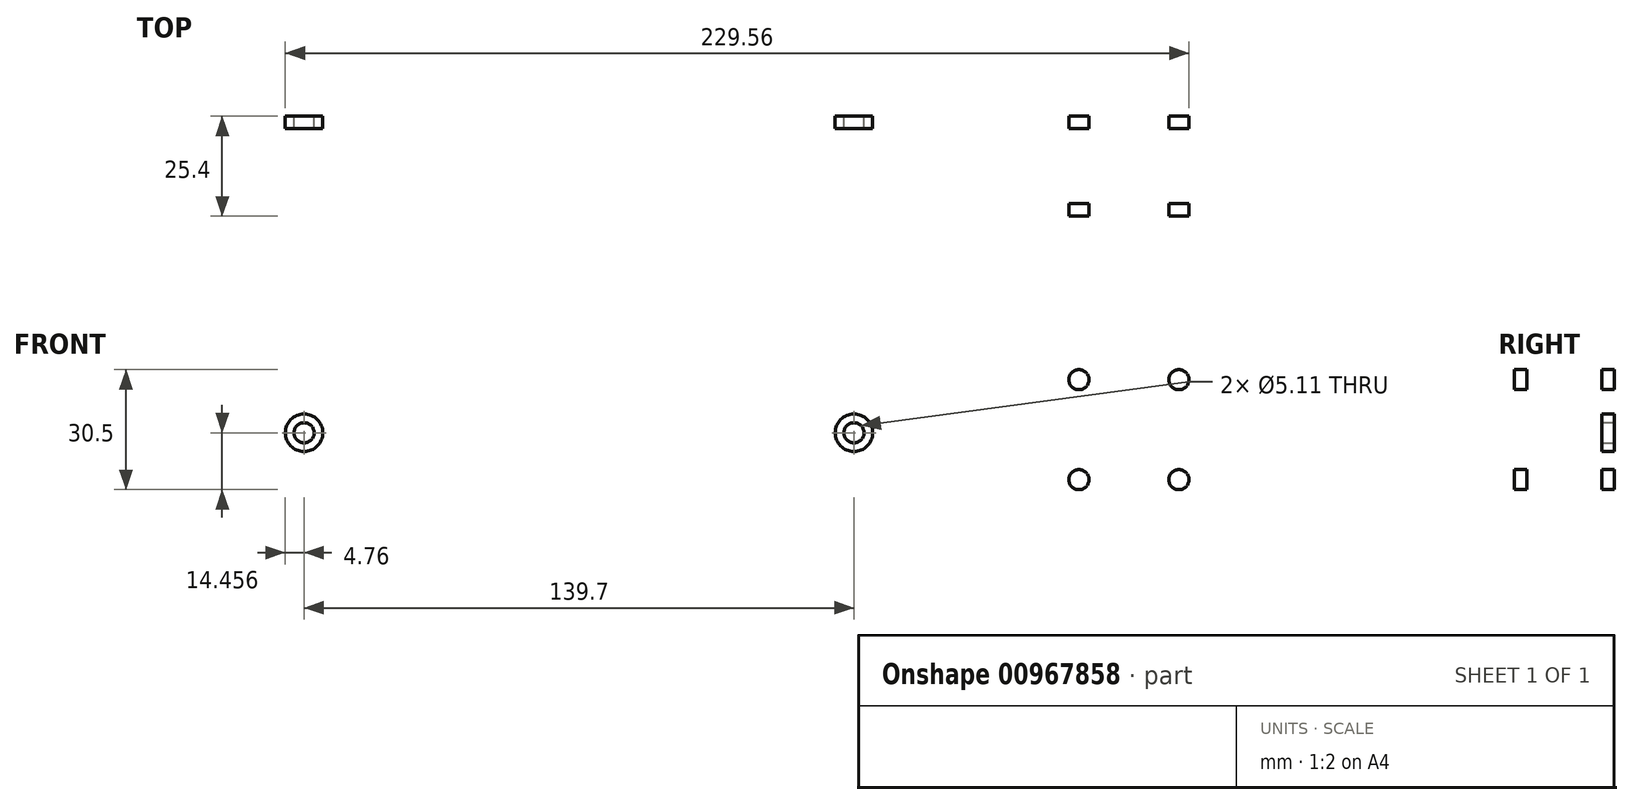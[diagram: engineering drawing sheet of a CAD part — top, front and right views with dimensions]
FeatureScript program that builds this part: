
annotation { "Feature Type Name" : "Feature", "Feature Type Description" : "" }
export const myFeature = defineFeature(function(context is Context, id is Id, definition is map)
    precondition{}
    {
        {
            var Q0;
            Q0=qCreatedBy(makeId("Front.planeOp"),FACE);
            var sketch = newSketch(context, id + "F0", { "sketchPlane" : qUnion([Q0])});
            skLineSegment(sketch, "E0.bottom", {"start": v(381, -25.4) * mm, "end": v(-381, -25.4) * mm});
            skLineSegment(sketch, "E0.top", {"start": v(381, 25.4) * mm, "end": v(-381, 25.4) * mm});
            skLineSegment(sketch, "E0.left", {"start": v(381, -25.4) * mm, "end": v(381, 25.4) * mm});
            skLineSegment(sketch, "E0.right", {"start": v(-381, -25.4) * mm, "end": v(-381, 25.4) * mm});
            skPoint(sketch, "E0.middle", {"position": v(0, 0) * mm});
            skLineSegment(sketch, "E1", {"start": v(-381, 0.8) * mm, "end": v(381, 0.8) * mm, "construction": true});
            skLineSegment(sketch, "E2", {"start": v(-381, -0.8) * mm, "end": v(381, -0.8) * mm, "construction": true});
            skLineSegment(sketch, "E3", {"start": v(0, 0.8) * mm, "end": v(0, -0.8) * mm, "construction": true});
            skCircle(sketch, "E4", {"center": v(-292.1, 0.8) * mm, "radius": 50.8 * mm, "construction": true});
            skCircle(sketch, "E5", {"center": v(292.1, 0.8) * mm, "radius": 50.8 * mm, "construction": true});
            skCircle(sketch, "E6", {"center": v(0, -0.8) * mm, "radius": 50.8 * mm, "construction": true});
            skLineSegment(sketch, "E7", {"start": v(-292.1, 0.8) * mm, "end": v(292.1, 0.8) * mm, "construction": true});
            skCircle(sketch, "E8", {"center": v(0, -0.8) * mm, "radius": 19.11 * mm});
            skCircle(sketch, "E9", {"center": v(-23.81, -0.8) * mm, "radius": 2.55 * mm});
            skCircle(sketch, "E10", {"center": v(23.81, -0.8) * mm, "radius": 2.55 * mm});
            skLineSegment(sketch, "E11", {"start": v(-23.81, -0.8) * mm, "end": v(23.81, -0.8) * mm});
            skLineSegment(sketch, "E12", {"start": v(23.81, -0.8) * mm, "end": v(-23.81, -0.8) * mm, "construction": true});
            skLineSegment(sketch, "E13.bottom", {"start": v(-273.05, -16.68) * mm, "end": v(-311.15, -16.68) * mm});
            skLineSegment(sketch, "E13.top", {"start": v(-273.05, 18.27) * mm, "end": v(-311.15, 18.27) * mm});
            skLineSegment(sketch, "E13.left", {"start": v(-269.88, -16.68) * mm, "end": v(-269.88, 18.27) * mm, "construction": true});
            skLineSegment(sketch, "E13.right", {"start": v(-314.33, -16.68) * mm, "end": v(-314.33, 18.27) * mm, "construction": true});
            skLineSegment(sketch, "E14", {"start": v(-314.33, 15.1) * mm, "end": v(-314.33, 3.35) * mm});
            skLineSegment(sketch, "E15", {"start": v(-314.33, 3.35) * mm, "end": v(-323.85, 3.35) * mm});
            skArc(sketch, "E16", {"start": v(-323.85, 3.35) * mm, "mid": v(-326.4, 0.8) * mm, "end": v(-323.85, -1.76) * mm});
            skLineSegment(sketch, "E17", {"start": v(-323.85, -1.76) * mm, "end": v(-314.33, -1.76) * mm});
            skLineSegment(sketch, "E18", {"start": v(-314.33, -1.76) * mm, "end": v(-314.33, -13.5) * mm});
            skLineSegment(sketch, "E19", {"start": v(-269.88, 3.35) * mm, "end": v(-260.35, 3.35) * mm});
            skLineSegment(sketch, "E20", {"start": v(-269.88, -1.76) * mm, "end": v(-260.35, -1.76) * mm});
            skArc(sketch, "E21", {"start": v(-260.35, -1.76) * mm, "mid": v(-257.8, 0.8) * mm, "end": v(-260.35, 3.35) * mm});
            skCircle(sketch, "E22", {"center": v(-247.65, 0.8) * mm, "radius": 2.55 * mm});
            skLineSegment(sketch, "E23", {"start": v(-269.88, 15.1) * mm, "end": v(-269.88, 3.35) * mm});
            skLineSegment(sketch, "E24", {"start": v(-269.88, -1.76) * mm, "end": v(-269.88, -13.5) * mm});
            skPoint(sketch, "E25.visualSharp", {"position": v(-314.33, 18.27) * mm});
            skArc(sketch, "E25.filletArc", {"start": v(-311.15, 18.27) * mm, "mid": v(-313.4, 17.34) * mm, "end": v(-314.33, 15.1) * mm});
            skPoint(sketch, "E26.visualSharp", {"position": v(-269.88, 18.27) * mm});
            skArc(sketch, "E26.filletArc", {"start": v(-269.88, 15.1) * mm, "mid": v(-270.8, 17.34) * mm, "end": v(-273.05, 18.27) * mm});
            skPoint(sketch, "E27.visualSharp", {"position": v(-269.88, -16.68) * mm});
            skArc(sketch, "E27.filletArc", {"start": v(-273.05, -16.68) * mm, "mid": v(-270.8, -15.75) * mm, "end": v(-269.88, -13.5) * mm});
            skPoint(sketch, "E28.visualSharp", {"position": v(-314.33, -16.68) * mm});
            skArc(sketch, "E28.filletArc", {"start": v(-314.33, -13.5) * mm, "mid": v(-313.4, -15.75) * mm, "end": v(-311.15, -16.68) * mm});
            skArc(sketch, "E29.MirrorCS", {"start": v(311.15, 18.27) * mm, "mid": v(313.4, 17.34) * mm, "end": v(314.33, 15.1) * mm});
            skArc(sketch, "E30.MirrorCS", {"start": v(323.85, 3.35) * mm, "mid": v(326.4, 0.8) * mm, "end": v(323.85, -1.76) * mm});
            skArc(sketch, "E31.MirrorCS", {"start": v(269.88, 15.1) * mm, "mid": v(270.8, 17.34) * mm, "end": v(273.05, 18.27) * mm});
            skArc(sketch, "E32.MirrorCS", {"start": v(314.33, -13.5) * mm, "mid": v(313.4, -15.75) * mm, "end": v(311.15, -16.68) * mm});
            skLineSegment(sketch, "E33.MirrorCS", {"start": v(314.33, 3.35) * mm, "end": v(323.85, 3.35) * mm});
            skLineSegment(sketch, "E34.MirrorCS", {"start": v(323.85, -1.76) * mm, "end": v(314.33, -1.76) * mm});
            skArc(sketch, "E35.MirrorCS", {"start": v(260.35, -1.76) * mm, "mid": v(257.8, 0.8) * mm, "end": v(260.35, 3.35) * mm});
            skArc(sketch, "E36.MirrorCS", {"start": v(273.05, -16.68) * mm, "mid": v(270.8, -15.75) * mm, "end": v(269.88, -13.5) * mm});
            skLineSegment(sketch, "E37.MirrorCS", {"start": v(269.88, 3.35) * mm, "end": v(260.35, 3.35) * mm});
            skCircle(sketch, "E38.MirrorC", {"center": v(247.65, 0.8) * mm, "radius": 2.55 * mm});
            skLineSegment(sketch, "E39.MirrorCS", {"start": v(314.33, -1.76) * mm, "end": v(314.33, -13.5) * mm});
            skLineSegment(sketch, "E40.MirrorCS", {"start": v(269.88, 15.1) * mm, "end": v(269.88, 3.35) * mm});
            skLineSegment(sketch, "E41.MirrorCS", {"start": v(314.33, 15.1) * mm, "end": v(314.33, 3.35) * mm});
            skLineSegment(sketch, "E42.MirrorCS", {"start": v(269.88, -1.76) * mm, "end": v(269.88, -13.5) * mm});
            skPoint(sketch, "E43.MirrorP", {"position": v(314.33, 18.27) * mm});
            skLineSegment(sketch, "E44.MirrorCS", {"start": v(269.88, -1.76) * mm, "end": v(260.35, -1.76) * mm});
            skPoint(sketch, "E45.MirrorP", {"position": v(314.33, -16.68) * mm});
            skLineSegment(sketch, "E46.MirrorCS", {"start": v(269.88, -16.68) * mm, "end": v(269.88, 18.27) * mm, "construction": true});
            skLineSegment(sketch, "E47.MirrorCS", {"start": v(314.33, -16.68) * mm, "end": v(314.33, 18.27) * mm, "construction": true});
            skPoint(sketch, "E48.MirrorP", {"position": v(269.88, 18.27) * mm});
            skLineSegment(sketch, "E49.MirrorCS", {"start": v(273.05, -16.68) * mm, "end": v(311.15, -16.68) * mm});
            skPoint(sketch, "E50.MirrorP", {"position": v(269.88, -16.68) * mm});
            skLineSegment(sketch, "E51.MirrorCS", {"start": v(273.05, 18.27) * mm, "end": v(311.15, 18.27) * mm});
            skCircle(sketch, "E52", {"center": v(69.85, -0.8) * mm, "radius": 2.55 * mm});
            skCircle(sketch, "E53", {"center": v(-69.85, -0.8) * mm, "radius": 2.55 * mm});
            skLineSegment(sketch, "E54", {"start": v(-69.85, -0.8) * mm, "end": v(69.85, -0.8) * mm, "construction": true});
            skSolve(sketch);
        }
        {
            var Q0;
            Q0=qSketchRegion(id+"F0",true);
            extrude(context, id + "F1", {"entities" : qUnion([Q0]), "depth" : 25.4 * mm, "offsetDistance" : 25.4 * mm});
        }
        {
            var Q0;
            Q0=makeQuery(id+"F1.opExtrude","SWEPT_FACE",FACE,{"disambiguationData":[OSD([sQuery(id+"F0.wireOp",EDGE,"E0.right")])]});
            var sketch = newSketch(context, id + "F2", { "sketchPlane" : qUnion([Q0])});
            skLineSegment(sketch, "E55.0", {"start": v(22.23, 22.23) * mm, "end": v(3.18, 22.23) * mm});
            skLineSegment(sketch, "E55.1", {"start": v(22.23, -22.22) * mm, "end": v(22.23, 22.23) * mm});
            skLineSegment(sketch, "E55.2", {"start": v(22.23, -22.22) * mm, "end": v(3.18, -22.22) * mm});
            skLineSegment(sketch, "E55.3", {"start": v(3.18, -22.22) * mm, "end": v(3.18, 22.23) * mm});
            skSolve(sketch);
        }
        {
            var Q0;
            Q0=makeQuery(id+"F2.imprint","IMPRINT",FACE,{"disambiguationData":[TD([[makeQuery(id+"F2.imprint","IMPRINT",EDGE,{"derivedFrom":sQuery(id+"F2.wireOp",EDGE,"E55.0")}),1.0]])]});
            extrude(context, id + "F3", {"entities" : qUnion([Q0]), "operationType" : NewBodyOperationType.REMOVE, "oppositeDirection" : true, "depth" : 762 * mm, "offsetDistance" : 25.4 * mm});
        }
        {
            var Q0;
            Q0=makeQuery(id+"F1.opExtrude","SWEPT_FACE",FACE,{"disambiguationData":[OSD([sQuery(id+"F0.wireOp",EDGE,"E0.top")])]});
            var sketch = newSketch(context, id + "F4", { "sketchPlane" : qUnion([Q0])});
            skCircle(sketch, "E56", {"center": v(-368.3, -12.7) * mm, "radius": 2.55 * mm});
            skPoint(sketch, "E56.centerSnap0", {"position": v(-381, -12.7) * mm});
            skCircle(sketch, "E57.1.0.0", {"center": v(-342.9, -12.7) * mm, "radius": 2.55 * mm});
            skCircle(sketch, "E57.2.0.0", {"center": v(-317.5, -12.7) * mm, "radius": 2.55 * mm});
            skCircle(sketch, "E57.3.0.0", {"center": v(-292.1, -12.7) * mm, "radius": 2.55 * mm});
            skCircle(sketch, "E57.4.0.0", {"center": v(-266.7, -12.7) * mm, "radius": 2.55 * mm});
            skCircle(sketch, "E57.5.0.0", {"center": v(-241.3, -12.7) * mm, "radius": 2.55 * mm});
            skCircle(sketch, "E57.6.0.0", {"center": v(-215.9, -12.7) * mm, "radius": 2.55 * mm});
            skCircle(sketch, "E57.7.0.0", {"center": v(-190.5, -12.7) * mm, "radius": 2.55 * mm});
            skCircle(sketch, "E57.8.0.0", {"center": v(-165.1, -12.7) * mm, "radius": 2.55 * mm});
            skCircle(sketch, "E57.9.0.0", {"center": v(-139.7, -12.7) * mm, "radius": 2.55 * mm});
            skCircle(sketch, "E57.10.0.0", {"center": v(-114.3, -12.7) * mm, "radius": 2.55 * mm});
            skCircle(sketch, "E57.11.0.0", {"center": v(-88.9, -12.7) * mm, "radius": 2.55 * mm});
            skCircle(sketch, "E57.12.0.0", {"center": v(-63.5, -12.7) * mm, "radius": 2.55 * mm});
            skCircle(sketch, "E57.13.0.0", {"center": v(-38.1, -12.7) * mm, "radius": 2.55 * mm});
            skCircle(sketch, "E57.14.0.0", {"center": v(-12.7, -12.7) * mm, "radius": 2.55 * mm});
            skCircle(sketch, "E57.15.0.0", {"center": v(12.7, -12.7) * mm, "radius": 2.55 * mm});
            skCircle(sketch, "E57.16.0.0", {"center": v(38.1, -12.7) * mm, "radius": 2.55 * mm});
            skCircle(sketch, "E57.17.0.0", {"center": v(63.5, -12.7) * mm, "radius": 2.55 * mm});
            skCircle(sketch, "E57.18.0.0", {"center": v(88.9, -12.7) * mm, "radius": 2.55 * mm});
            skCircle(sketch, "E57.19.0.0", {"center": v(114.3, -12.7) * mm, "radius": 2.55 * mm});
            skCircle(sketch, "E57.20.0.0", {"center": v(139.7, -12.7) * mm, "radius": 2.55 * mm});
            skCircle(sketch, "E57.21.0.0", {"center": v(165.1, -12.7) * mm, "radius": 2.55 * mm});
            skCircle(sketch, "E57.22.0.0", {"center": v(190.5, -12.7) * mm, "radius": 2.55 * mm});
            skCircle(sketch, "E57.23.0.0", {"center": v(215.9, -12.7) * mm, "radius": 2.55 * mm});
            skCircle(sketch, "E57.24.0.0", {"center": v(241.3, -12.7) * mm, "radius": 2.55 * mm});
            skCircle(sketch, "E57.25.0.0", {"center": v(266.7, -12.7) * mm, "radius": 2.55 * mm});
            skCircle(sketch, "E57.26.0.0", {"center": v(292.1, -12.7) * mm, "radius": 2.55 * mm});
            skCircle(sketch, "E57.27.0.0", {"center": v(317.5, -12.7) * mm, "radius": 2.55 * mm});
            skCircle(sketch, "E57.28.0.0", {"center": v(342.9, -12.7) * mm, "radius": 2.55 * mm});
            skCircle(sketch, "E57.29.0.0", {"center": v(368.3, -12.7) * mm, "radius": 2.55 * mm});
            skLineSegment(sketch, "E57.direction1", {"start": v(-368.3, -12.7) * mm, "end": v(-342.9, -12.7) * mm, "construction": true});
            skSolve(sketch);
        }
        {
            var Q0;
            Q0=sQuery(id+"F4.wireOp",VERTEX,"E57.22.0.0.center");
            var Q1;
            Q1=sQuery(id+"F4.wireOp",VERTEX,"E57.16.0.0.center");
            var Q2;
            Q2=sQuery(id+"F4.wireOp",VERTEX,"E57.23.0.0.center");
            var Q3;
            Q3=sQuery(id+"F4.wireOp",VERTEX,"E57.17.0.0.center");
            var Q4;
            Q4=sQuery(id+"F4.wireOp",VERTEX,"E57.26.0.0.center");
            var Q5;
            Q5=sQuery(id+"F4.wireOp",VERTEX,"E57.20.0.0.center");
            var Q6;
            Q6=sQuery(id+"F4.wireOp",VERTEX,"E57.13.0.0.center");
            var Q7;
            Q7=sQuery(id+"F4.wireOp",VERTEX,"E57.29.0.0.center");
            var Q8;
            Q8=sQuery(id+"F4.wireOp",VERTEX,"E57.24.0.0.center");
            var Q9;
            Q9=sQuery(id+"F4.wireOp",VERTEX,"E57.10.0.0.center");
            var Q10;
            Q10=sQuery(id+"F4.wireOp",VERTEX,"E57.18.0.0.center");
            var Q11;
            Q11=sQuery(id+"F4.wireOp",VERTEX,"E57.11.0.0.center");
            var Q12;
            Q12=sQuery(id+"F4.wireOp",VERTEX,"E57.27.0.0.center");
            var Q13;
            Q13=sQuery(id+"F4.wireOp",VERTEX,"E57.12.0.0.center");
            var Q14;
            Q14=sQuery(id+"F4.wireOp",VERTEX,"E57.14.0.0.center");
            var Q15;
            Q15=sQuery(id+"F4.wireOp",VERTEX,"E57.1.0.0.center");
            var Q16;
            Q16=sQuery(id+"F4.wireOp",VERTEX,"E57.2.0.0.center");
            var Q17;
            Q17=sQuery(id+"F4.wireOp",VERTEX,"E57.3.0.0.center");
            var Q18;
            Q18=sQuery(id+"F4.wireOp",VERTEX,"E57.4.0.0.center");
            var Q19;
            Q19=sQuery(id+"F4.wireOp",VERTEX,"E57.5.0.0.center");
            var Q20;
            Q20=sQuery(id+"F4.wireOp",VERTEX,"E57.6.0.0.center");
            var Q21;
            Q21=sQuery(id+"F4.wireOp",VERTEX,"E57.7.0.0.center");
            var Q22;
            Q22=sQuery(id+"F4.wireOp",VERTEX,"E57.8.0.0.center");
            var Q23;
            Q23=sQuery(id+"F4.wireOp",VERTEX,"E57.9.0.0.center");
            var Q24;
            Q24=sQuery(id+"F4.wireOp",VERTEX,"E57.25.0.0.center");
            var Q25;
            Q25=sQuery(id+"F4.wireOp",VERTEX,"E57.21.0.0.center");
            var Q26;
            Q26=sQuery(id+"F4.wireOp",VERTEX,"E57.19.0.0.center");
            var Q27;
            Q27=sQuery(id+"F4.wireOp",VERTEX,"E57.28.0.0.center");
            var Q28;
            Q28=sQuery(id+"F4.wireOp",VERTEX,"E57.15.0.0.center");
            var Q29;
            Q29=sQuery(id+"F4.wireOp",VERTEX,"E56.center");
            var Q30;
            Q30=makeQuery(id+"F1.opExtrude","SWEPT_BODY",BODY,{"disambiguationData":[OSD([sQuery(id+"F0.wireOp",EDGE,"E0.bottom"),sQuery(id+"F0.wireOp",EDGE,"E0.top"),sQuery(id+"F0.wireOp",EDGE,"E0.right"),sQuery(id+"F0.wireOp",EDGE,"E8"),sQuery(id+"F0.wireOp",EDGE,"E9"),sQuery(id+"F0.wireOp",EDGE,"E10"),sQuery(id+"F0.wireOp",EDGE,"E13.bottom"),sQuery(id+"F0.wireOp",EDGE,"E13.top"),sQuery(id+"F0.wireOp",EDGE,"E14"),sQuery(id+"F0.wireOp",EDGE,"E15"),sQuery(id+"F0.wireOp",EDGE,"E16"),sQuery(id+"F0.wireOp",EDGE,"E17"),sQuery(id+"F0.wireOp",EDGE,"E18"),sQuery(id+"F0.wireOp",EDGE,"E19"),sQuery(id+"F0.wireOp",EDGE,"E20"),sQuery(id+"F0.wireOp",EDGE,"E21"),sQuery(id+"F0.wireOp",EDGE,"E22"),sQuery(id+"F0.wireOp",EDGE,"E23"),sQuery(id+"F0.wireOp",EDGE,"E24"),sQuery(id+"F0.wireOp",EDGE,"E25.filletArc"),sQuery(id+"F0.wireOp",EDGE,"E26.filletArc"),sQuery(id+"F0.wireOp",EDGE,"E27.filletArc"),sQuery(id+"F0.wireOp",EDGE,"E28.filletArc"),sQuery(id+"F0.wireOp",EDGE,"E29.MirrorCS"),sQuery(id+"F0.wireOp",EDGE,"E30.MirrorCS"),sQuery(id+"F0.wireOp",EDGE,"E31.MirrorCS"),sQuery(id+"F0.wireOp",EDGE,"E32.MirrorCS"),sQuery(id+"F0.wireOp",EDGE,"E33.MirrorCS"),sQuery(id+"F0.wireOp",EDGE,"E34.MirrorCS"),sQuery(id+"F0.wireOp",EDGE,"E35.MirrorCS"),sQuery(id+"F0.wireOp",EDGE,"E36.MirrorCS"),sQuery(id+"F0.wireOp",EDGE,"E37.MirrorCS"),sQuery(id+"F0.wireOp",EDGE,"E38.MirrorC"),sQuery(id+"F0.wireOp",EDGE,"E39.MirrorCS"),sQuery(id+"F0.wireOp",EDGE,"E40.MirrorCS"),sQuery(id+"F0.wireOp",EDGE,"E41.MirrorCS"),sQuery(id+"F0.wireOp",EDGE,"E42.MirrorCS"),sQuery(id+"F0.wireOp",EDGE,"E44.MirrorCS"),sQuery(id+"F0.wireOp",EDGE,"E49.MirrorCS"),sQuery(id+"F0.wireOp",EDGE,"E51.MirrorCS"),sQuery(id+"F0.wireOp",EDGE,"E0.left"),sQuery(id+"F0.wireOp",EDGE,"E52"),sQuery(id+"F0.wireOp",EDGE,"E53")])]});
            hole(context, id + "F5", {"style" : HoleStyle.SIMPLE, "endStyle" : HoleEndStyle.BLIND, "holeDiameter" : 5.1 * mm, "majorDiameter" : 6.35 * mm, "holeDepth" : 50.8 * mm, "isTappedThrough" : true, "tappedDepth" : 12.7 * mm, "tapClearance" : 3, "startFromSketch" : true, "locations" : qUnion([Q0, Q1, Q2, Q3, Q4, Q5, Q6, Q7, Q8, Q9, Q10, Q11, Q12, Q13, Q14, Q15, Q16, Q17, Q18, Q19, Q20, Q21, Q22, Q23, Q24, Q25, Q26, Q27, Q28, Q29]), "scope" : qUnion([Q30])});
        }
        {
            var Q0;
            Q0=makeQuery(id+"F1.opExtrude","CAP_FACE",FACE,{"disambiguationData":[OSD([sQuery(id+"F0.wireOp",EDGE,"E0.bottom"),sQuery(id+"F0.wireOp",EDGE,"E0.top"),sQuery(id+"F0.wireOp",EDGE,"E0.right"),sQuery(id+"F0.wireOp",EDGE,"E8"),sQuery(id+"F0.wireOp",EDGE,"E9"),sQuery(id+"F0.wireOp",EDGE,"E10"),sQuery(id+"F0.wireOp",EDGE,"E13.bottom"),sQuery(id+"F0.wireOp",EDGE,"E13.top"),sQuery(id+"F0.wireOp",EDGE,"E14"),sQuery(id+"F0.wireOp",EDGE,"E15"),sQuery(id+"F0.wireOp",EDGE,"E16"),sQuery(id+"F0.wireOp",EDGE,"E17"),sQuery(id+"F0.wireOp",EDGE,"E18"),sQuery(id+"F0.wireOp",EDGE,"E19"),sQuery(id+"F0.wireOp",EDGE,"E20"),sQuery(id+"F0.wireOp",EDGE,"E21"),sQuery(id+"F0.wireOp",EDGE,"E22"),sQuery(id+"F0.wireOp",EDGE,"E23"),sQuery(id+"F0.wireOp",EDGE,"E24"),sQuery(id+"F0.wireOp",EDGE,"E25.filletArc"),sQuery(id+"F0.wireOp",EDGE,"E26.filletArc"),sQuery(id+"F0.wireOp",EDGE,"E27.filletArc"),sQuery(id+"F0.wireOp",EDGE,"E28.filletArc"),sQuery(id+"F0.wireOp",EDGE,"E29.MirrorCS"),sQuery(id+"F0.wireOp",EDGE,"E30.MirrorCS"),sQuery(id+"F0.wireOp",EDGE,"E31.MirrorCS"),sQuery(id+"F0.wireOp",EDGE,"E32.MirrorCS"),sQuery(id+"F0.wireOp",EDGE,"E33.MirrorCS"),sQuery(id+"F0.wireOp",EDGE,"E34.MirrorCS"),sQuery(id+"F0.wireOp",EDGE,"E35.MirrorCS"),sQuery(id+"F0.wireOp",EDGE,"E36.MirrorCS"),sQuery(id+"F0.wireOp",EDGE,"E37.MirrorCS"),sQuery(id+"F0.wireOp",EDGE,"E38.MirrorC"),sQuery(id+"F0.wireOp",EDGE,"E39.MirrorCS"),sQuery(id+"F0.wireOp",EDGE,"E40.MirrorCS"),sQuery(id+"F0.wireOp",EDGE,"E41.MirrorCS"),sQuery(id+"F0.wireOp",EDGE,"E42.MirrorCS"),sQuery(id+"F0.wireOp",EDGE,"E44.MirrorCS"),sQuery(id+"F0.wireOp",EDGE,"E49.MirrorCS"),sQuery(id+"F0.wireOp",EDGE,"E51.MirrorCS"),sQuery(id+"F0.wireOp",EDGE,"E0.left"),sQuery(id+"F0.wireOp",EDGE,"E52"),sQuery(id+"F0.wireOp",EDGE,"E53")])],"isStart":false});
            var sketch = newSketch(context, id + "F6", { "sketchPlane" : qUnion([Q0])});
            skCircle(sketch, "E58", {"center": v(-69.85, -0.8) * mm, "radius": 4.76 * mm});
            skCircle(sketch, "E59", {"center": v(69.85, -0.8) * mm, "radius": 4.76 * mm});
            skSolve(sketch);
        }
        {
            var Q0;
            Q0=sQuery(id+"F6.wireOp",VERTEX,"E58.center");
            var Q1;
            Q1=sQuery(id+"F6.wireOp",VERTEX,"E59.center");
            var Q2;
            Q2=makeQuery(id+"F1.opExtrude","SWEPT_BODY",BODY,{"disambiguationData":[OSD([sQuery(id+"F0.wireOp",EDGE,"E0.bottom"),sQuery(id+"F0.wireOp",EDGE,"E0.top"),sQuery(id+"F0.wireOp",EDGE,"E0.right"),sQuery(id+"F0.wireOp",EDGE,"E8"),sQuery(id+"F0.wireOp",EDGE,"E9"),sQuery(id+"F0.wireOp",EDGE,"E10"),sQuery(id+"F0.wireOp",EDGE,"E13.bottom"),sQuery(id+"F0.wireOp",EDGE,"E13.top"),sQuery(id+"F0.wireOp",EDGE,"E14"),sQuery(id+"F0.wireOp",EDGE,"E15"),sQuery(id+"F0.wireOp",EDGE,"E16"),sQuery(id+"F0.wireOp",EDGE,"E17"),sQuery(id+"F0.wireOp",EDGE,"E18"),sQuery(id+"F0.wireOp",EDGE,"E19"),sQuery(id+"F0.wireOp",EDGE,"E20"),sQuery(id+"F0.wireOp",EDGE,"E21"),sQuery(id+"F0.wireOp",EDGE,"E22"),sQuery(id+"F0.wireOp",EDGE,"E23"),sQuery(id+"F0.wireOp",EDGE,"E24"),sQuery(id+"F0.wireOp",EDGE,"E25.filletArc"),sQuery(id+"F0.wireOp",EDGE,"E26.filletArc"),sQuery(id+"F0.wireOp",EDGE,"E27.filletArc"),sQuery(id+"F0.wireOp",EDGE,"E28.filletArc"),sQuery(id+"F0.wireOp",EDGE,"E29.MirrorCS"),sQuery(id+"F0.wireOp",EDGE,"E30.MirrorCS"),sQuery(id+"F0.wireOp",EDGE,"E31.MirrorCS"),sQuery(id+"F0.wireOp",EDGE,"E32.MirrorCS"),sQuery(id+"F0.wireOp",EDGE,"E33.MirrorCS"),sQuery(id+"F0.wireOp",EDGE,"E34.MirrorCS"),sQuery(id+"F0.wireOp",EDGE,"E35.MirrorCS"),sQuery(id+"F0.wireOp",EDGE,"E36.MirrorCS"),sQuery(id+"F0.wireOp",EDGE,"E37.MirrorCS"),sQuery(id+"F0.wireOp",EDGE,"E38.MirrorC"),sQuery(id+"F0.wireOp",EDGE,"E39.MirrorCS"),sQuery(id+"F0.wireOp",EDGE,"E40.MirrorCS"),sQuery(id+"F0.wireOp",EDGE,"E41.MirrorCS"),sQuery(id+"F0.wireOp",EDGE,"E42.MirrorCS"),sQuery(id+"F0.wireOp",EDGE,"E44.MirrorCS"),sQuery(id+"F0.wireOp",EDGE,"E49.MirrorCS"),sQuery(id+"F0.wireOp",EDGE,"E51.MirrorCS"),sQuery(id+"F0.wireOp",EDGE,"E0.left"),sQuery(id+"F0.wireOp",EDGE,"E52"),sQuery(id+"F0.wireOp",EDGE,"E53")])]});
            hole(context, id + "F7", {"style" : HoleStyle.SIMPLE, "endStyle" : HoleEndStyle.BLIND, "holeDiameter" : 9.52 * mm, "majorDiameter" : 6.35 * mm, "holeDepth" : 3.17 * mm, "isTappedThrough" : true, "tappedDepth" : 12.7 * mm, "tapClearance" : 3, "startFromSketch" : true, "locations" : qUnion([Q0, Q1]), "scope" : qUnion([Q2])});
        }
        {
            var Q0;
            Q0=makeQuery(id+"F1.opExtrude","CAP_FACE",FACE,{"disambiguationData":[OSD([sQuery(id+"F0.wireOp",EDGE,"E0.bottom"),sQuery(id+"F0.wireOp",EDGE,"E0.top"),sQuery(id+"F0.wireOp",EDGE,"E0.right"),sQuery(id+"F0.wireOp",EDGE,"E8"),sQuery(id+"F0.wireOp",EDGE,"E9"),sQuery(id+"F0.wireOp",EDGE,"E10"),sQuery(id+"F0.wireOp",EDGE,"E13.bottom"),sQuery(id+"F0.wireOp",EDGE,"E13.top"),sQuery(id+"F0.wireOp",EDGE,"E14"),sQuery(id+"F0.wireOp",EDGE,"E15"),sQuery(id+"F0.wireOp",EDGE,"E16"),sQuery(id+"F0.wireOp",EDGE,"E17"),sQuery(id+"F0.wireOp",EDGE,"E18"),sQuery(id+"F0.wireOp",EDGE,"E19"),sQuery(id+"F0.wireOp",EDGE,"E20"),sQuery(id+"F0.wireOp",EDGE,"E21"),sQuery(id+"F0.wireOp",EDGE,"E22"),sQuery(id+"F0.wireOp",EDGE,"E23"),sQuery(id+"F0.wireOp",EDGE,"E24"),sQuery(id+"F0.wireOp",EDGE,"E25.filletArc"),sQuery(id+"F0.wireOp",EDGE,"E26.filletArc"),sQuery(id+"F0.wireOp",EDGE,"E27.filletArc"),sQuery(id+"F0.wireOp",EDGE,"E28.filletArc"),sQuery(id+"F0.wireOp",EDGE,"E29.MirrorCS"),sQuery(id+"F0.wireOp",EDGE,"E30.MirrorCS"),sQuery(id+"F0.wireOp",EDGE,"E31.MirrorCS"),sQuery(id+"F0.wireOp",EDGE,"E32.MirrorCS"),sQuery(id+"F0.wireOp",EDGE,"E33.MirrorCS"),sQuery(id+"F0.wireOp",EDGE,"E34.MirrorCS"),sQuery(id+"F0.wireOp",EDGE,"E35.MirrorCS"),sQuery(id+"F0.wireOp",EDGE,"E36.MirrorCS"),sQuery(id+"F0.wireOp",EDGE,"E37.MirrorCS"),sQuery(id+"F0.wireOp",EDGE,"E38.MirrorC"),sQuery(id+"F0.wireOp",EDGE,"E39.MirrorCS"),sQuery(id+"F0.wireOp",EDGE,"E40.MirrorCS"),sQuery(id+"F0.wireOp",EDGE,"E41.MirrorCS"),sQuery(id+"F0.wireOp",EDGE,"E42.MirrorCS"),sQuery(id+"F0.wireOp",EDGE,"E44.MirrorCS"),sQuery(id+"F0.wireOp",EDGE,"E49.MirrorCS"),sQuery(id+"F0.wireOp",EDGE,"E51.MirrorCS"),sQuery(id+"F0.wireOp",EDGE,"E0.left"),sQuery(id+"F0.wireOp",EDGE,"E52"),sQuery(id+"F0.wireOp",EDGE,"E53")])],"isStart":false});
            var sketch = newSketch(context, id + "F8", { "sketchPlane" : qUnion([Q0])});
            skLineSegment(sketch, "E60.bottom", {"start": v(-152.4, 12.7) * mm, "end": v(-127, 12.7) * mm, "construction": true});
            skLineSegment(sketch, "E60.top", {"start": v(-152.4, -12.7) * mm, "end": v(-127, -12.7) * mm, "construction": true});
            skLineSegment(sketch, "E60.left", {"start": v(-152.4, 12.7) * mm, "end": v(-152.4, -12.7) * mm, "construction": true});
            skLineSegment(sketch, "E60.right", {"start": v(-127, 12.7) * mm, "end": v(-127, -12.7) * mm, "construction": true});
            skPoint(sketch, "E60.middle", {"position": v(-139.7, 0) * mm});
            skCircle(sketch, "E61", {"center": v(-152.4, 12.7) * mm, "radius": 2.55 * mm});
            skCircle(sketch, "E62", {"center": v(-127, 12.7) * mm, "radius": 2.55 * mm});
            skCircle(sketch, "E63", {"center": v(-152.4, -12.7) * mm, "radius": 2.55 * mm});
            skCircle(sketch, "E64", {"center": v(-127, -12.7) * mm, "radius": 2.55 * mm});
            skLineSegment(sketch, "E65", {"start": v(0, 25.4) * mm, "end": v(0, -25.4) * mm, "construction": true});
            skCircle(sketch, "E66.MirrorC", {"center": v(127, 12.7) * mm, "radius": 2.55 * mm});
            skCircle(sketch, "E67.MirrorC", {"center": v(152.4, -12.7) * mm, "radius": 2.55 * mm});
            skCircle(sketch, "E68.MirrorC", {"center": v(127, -12.7) * mm, "radius": 2.55 * mm});
            skCircle(sketch, "E69.MirrorC", {"center": v(152.4, 12.7) * mm, "radius": 2.55 * mm});
            skLineSegment(sketch, "E70.MirrorCS", {"start": v(127, 12.7) * mm, "end": v(127, -12.7) * mm, "construction": true});
            skLineSegment(sketch, "E71.MirrorCS", {"start": v(152.4, 12.7) * mm, "end": v(127, 12.7) * mm, "construction": true});
            skLineSegment(sketch, "E72.MirrorCS", {"start": v(152.4, 12.7) * mm, "end": v(152.4, -12.7) * mm, "construction": true});
            skPoint(sketch, "E73.MirrorP", {"position": v(139.7, 0) * mm});
            skLineSegment(sketch, "E74.MirrorCS", {"start": v(152.4, -12.7) * mm, "end": v(127, -12.7) * mm, "construction": true});
            skSolve(sketch);
        }
        {
            var Q0;
            Q0=makeQuery(id+"F8.imprint","IMPRINT",FACE,{"disambiguationData":[TD([[makeQuery(id+"F8.imprint","IMPRINT",EDGE,{"derivedFrom":sQuery(id+"F8.wireOp",EDGE,"E63")}),1.0]])]});
            var Q1;
            Q1=makeQuery(id+"F8.imprint","IMPRINT",FACE,{"disambiguationData":[TD([[makeQuery(id+"F8.imprint","IMPRINT",EDGE,{"derivedFrom":sQuery(id+"F8.wireOp",EDGE,"E61")}),1.0]])]});
            var Q2;
            Q2=makeQuery(id+"F8.imprint","IMPRINT",FACE,{"disambiguationData":[TD([[makeQuery(id+"F8.imprint","IMPRINT",EDGE,{"derivedFrom":sQuery(id+"F8.wireOp",EDGE,"E62")}),1.0]])]});
            var Q3;
            Q3=makeQuery(id+"F8.imprint","IMPRINT",FACE,{"disambiguationData":[TD([[makeQuery(id+"F8.imprint","IMPRINT",EDGE,{"derivedFrom":sQuery(id+"F8.wireOp",EDGE,"E64")}),1.0]])]});
            var Q4;
            Q4=makeQuery(id+"F8.imprint","IMPRINT",FACE,{"disambiguationData":[TD([[makeQuery(id+"F8.imprint","IMPRINT",EDGE,{"derivedFrom":sQuery(id+"F8.wireOp",EDGE,"E68.MirrorC")}),-1.0]])]});
            var Q5;
            Q5=makeQuery(id+"F8.imprint","IMPRINT",FACE,{"disambiguationData":[TD([[makeQuery(id+"F8.imprint","IMPRINT",EDGE,{"derivedFrom":sQuery(id+"F8.wireOp",EDGE,"E66.MirrorC")}),-1.0]])]});
            var Q6;
            Q6=makeQuery(id+"F8.imprint","IMPRINT",FACE,{"disambiguationData":[TD([[makeQuery(id+"F8.imprint","IMPRINT",EDGE,{"derivedFrom":sQuery(id+"F8.wireOp",EDGE,"E67.MirrorC")}),-1.0]])]});
            var Q7;
            Q7=makeQuery(id+"F8.imprint","IMPRINT",FACE,{"disambiguationData":[TD([[makeQuery(id+"F8.imprint","IMPRINT",EDGE,{"derivedFrom":sQuery(id+"F8.wireOp",EDGE,"E69.MirrorC")}),-1.0]])]});
            extrude(context, id + "F9", {"entities" : qUnion([Q0, Q1, Q2, Q3, Q4, Q5, Q6, Q7]), "operationType" : NewBodyOperationType.REMOVE, "oppositeDirection" : true, "depth" : 25.4 * mm, "offsetDistance" : 25.4 * mm});
        }
    });
